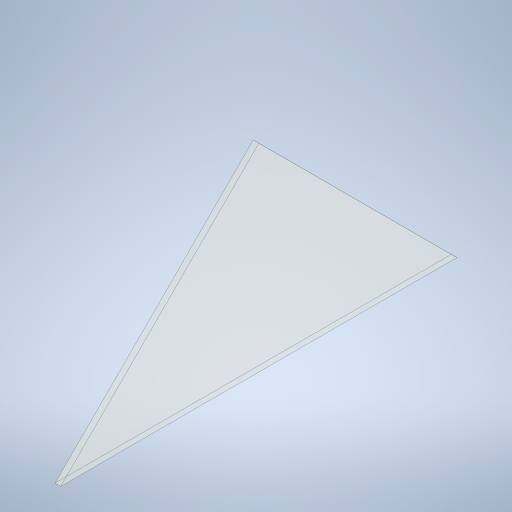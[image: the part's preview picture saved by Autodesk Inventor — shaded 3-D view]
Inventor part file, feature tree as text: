
AUTODESK INVENTOR PART (.ipt)
format: ipt  version: 2024 (Build 280153000, 153)  size: 230,912 bytes
history: native  units: in
note: dims shown in document units (in); Inventor stores cm internally (conversion verified against a paired STEP export)
features: extrude x1, sketch x1
ambient origin geometry x8: Origin, YZ Plane, XZ Plane, XY Plane, X Axis, Y Axis, Z Axis, Center Point
bodies: Solid1 (feature_tree)
feature tree (2):
  extrude  "Extrusion1"  TaperAngle=45.0deg  [1 undecoded]
  sketch  "Sketch1"  dims[d1=300.0in d2=45.0deg d3=4.25in d4=0.0in]
note: 1 required parameter value undecoded (feature->parameter linkage not recoverable at this tier; creation-order binding heuristic only, values carry confidence <= 0.55)
